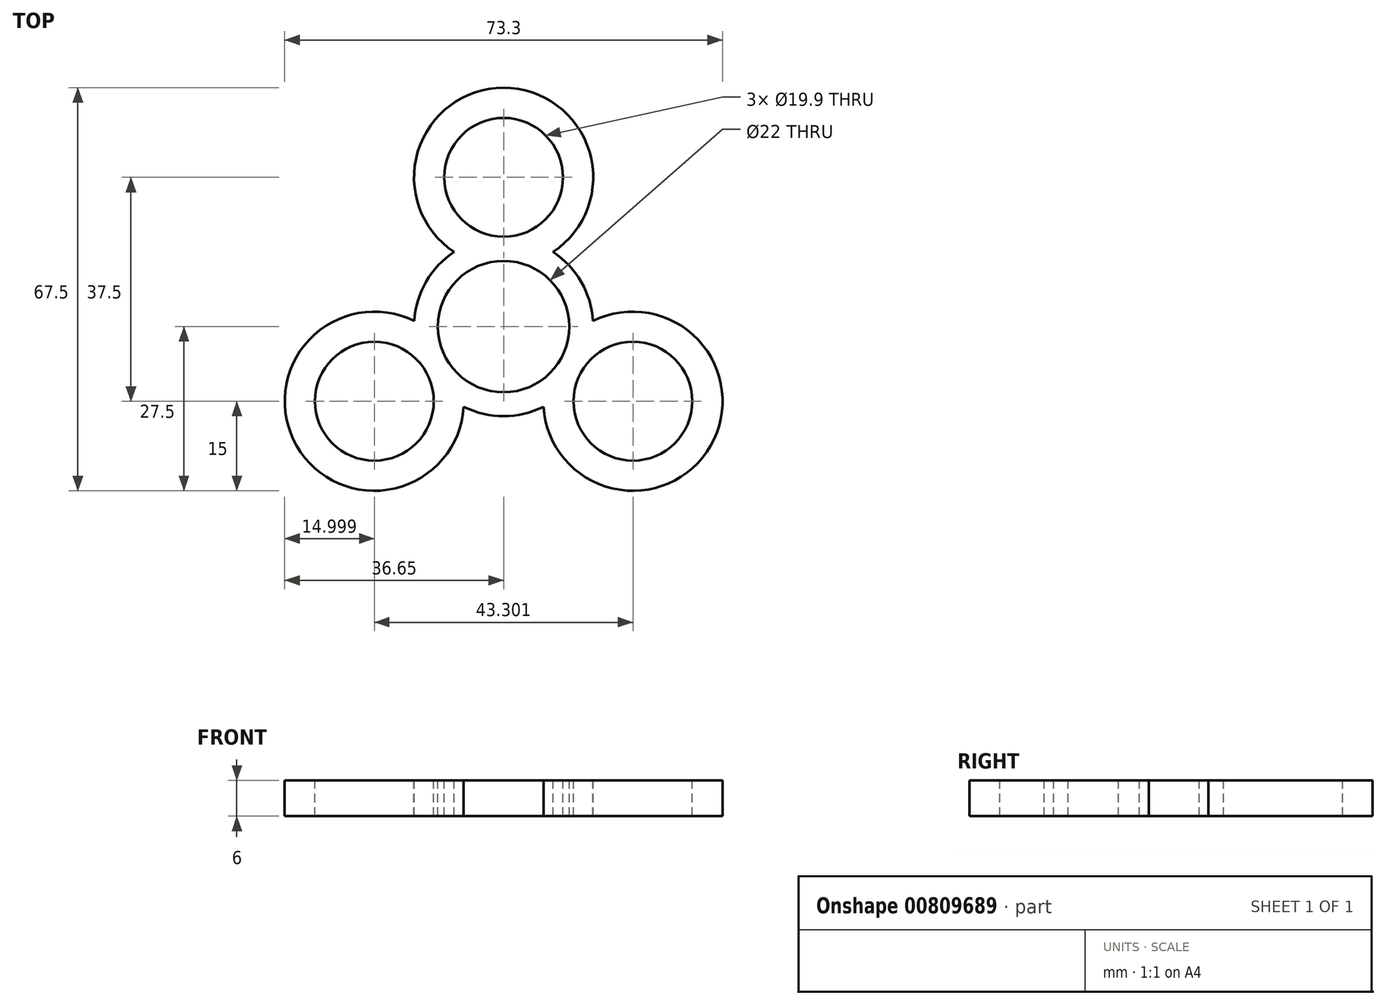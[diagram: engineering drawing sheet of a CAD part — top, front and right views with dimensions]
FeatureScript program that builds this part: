
annotation { "Feature Type Name" : "Feature", "Feature Type Description" : "" }
export const myFeature = defineFeature(function(context is Context, id is Id, definition is map)
    precondition{}
    {
        {
            var Q0;
            Q0=qCreatedBy(makeId("Top.planeOp"),FACE);
            var sketch = newSketch(context, id + "F0", { "sketchPlane" : qUnion([Q0])});
            skArc(sketch, "E0", {"start": v(9.53, 5.5) * mm, "mid": v(0, 11) * mm, "end": v(-9.53, 5.5) * mm});
            skCircle(sketch, "E1", {"center": v(0, 25) * mm, "radius": 9.95 * mm});
            skArc(sketch, "E2", {"start": v(-8.3, 12.5) * mm, "mid": v(-10.93, 10.27) * mm, "end": v(-13, 7.5) * mm});
            skArc(sketch, "E3.trimOffspring", {"start": v(8.3, 12.5) * mm, "mid": v(0, 40) * mm, "end": v(-8.3, 12.5) * mm});
            skArc(sketch, "E4.trimOffspring", {"start": v(13, 7.5) * mm, "mid": v(10.93, 10.27) * mm, "end": v(8.3, 12.5) * mm});
            skArc(sketch, "E5.1.0", {"start": v(-14.97, 0.93) * mm, "mid": v(-34.64, -20) * mm, "end": v(-6.68, -13.43) * mm});
            skCircle(sketch, "E5.1.1", {"center": v(-21.65, -12.5) * mm, "radius": 9.95 * mm});
            skArc(sketch, "E5.1.2", {"start": v(-6.68, -13.43) * mm, "mid": v(-3.43, -14.6) * mm, "end": v(0, -15) * mm});
            skArc(sketch, "E5.1.3", {"start": v(-13, 7.5) * mm, "mid": v(-14.36, 4.33) * mm, "end": v(-14.97, 0.93) * mm});
            skArc(sketch, "E5.1.4", {"start": v(-9.53, 5.5) * mm, "mid": v(-9.53, -5.5) * mm, "end": v(0, -11) * mm});
            skArc(sketch, "E5.2.0", {"start": v(6.68, -13.43) * mm, "mid": v(34.64, -20) * mm, "end": v(14.97, 0.93) * mm});
            skCircle(sketch, "E5.2.1", {"center": v(21.65, -12.5) * mm, "radius": 9.95 * mm});
            skArc(sketch, "E5.2.2", {"start": v(14.97, 0.93) * mm, "mid": v(14.36, 4.33) * mm, "end": v(13, 7.5) * mm});
            skArc(sketch, "E5.2.3", {"start": v(0, -15) * mm, "mid": v(3.43, -14.6) * mm, "end": v(6.68, -13.43) * mm});
            skArc(sketch, "E5.2.4", {"start": v(0, -11) * mm, "mid": v(9.53, -5.5) * mm, "end": v(9.53, 5.5) * mm});
            skSolve(sketch);
        }
        {
            var Q0;
            Q0 = qSketchRegion(id + "FWTHnqLZlqEd10H_0", true);
            var Q1;
            Q1=makeQuery(id+"F0.imprint","IMPRINT",FACE,{"disambiguationData":[TD([[makeQuery(id+"F0.imprint","IMPRINT",EDGE,{"derivedFrom":sQuery(id+"F0.wireOp",EDGE,"E0")}),-1.0]])]});
            extrude(context, id + "F1", {"entities" : qUnion([Q0, Q1]), "oppositeDirection" : true, "depth" : 6 * mm, "offsetDistance" : 25 * mm});
        }
    });
